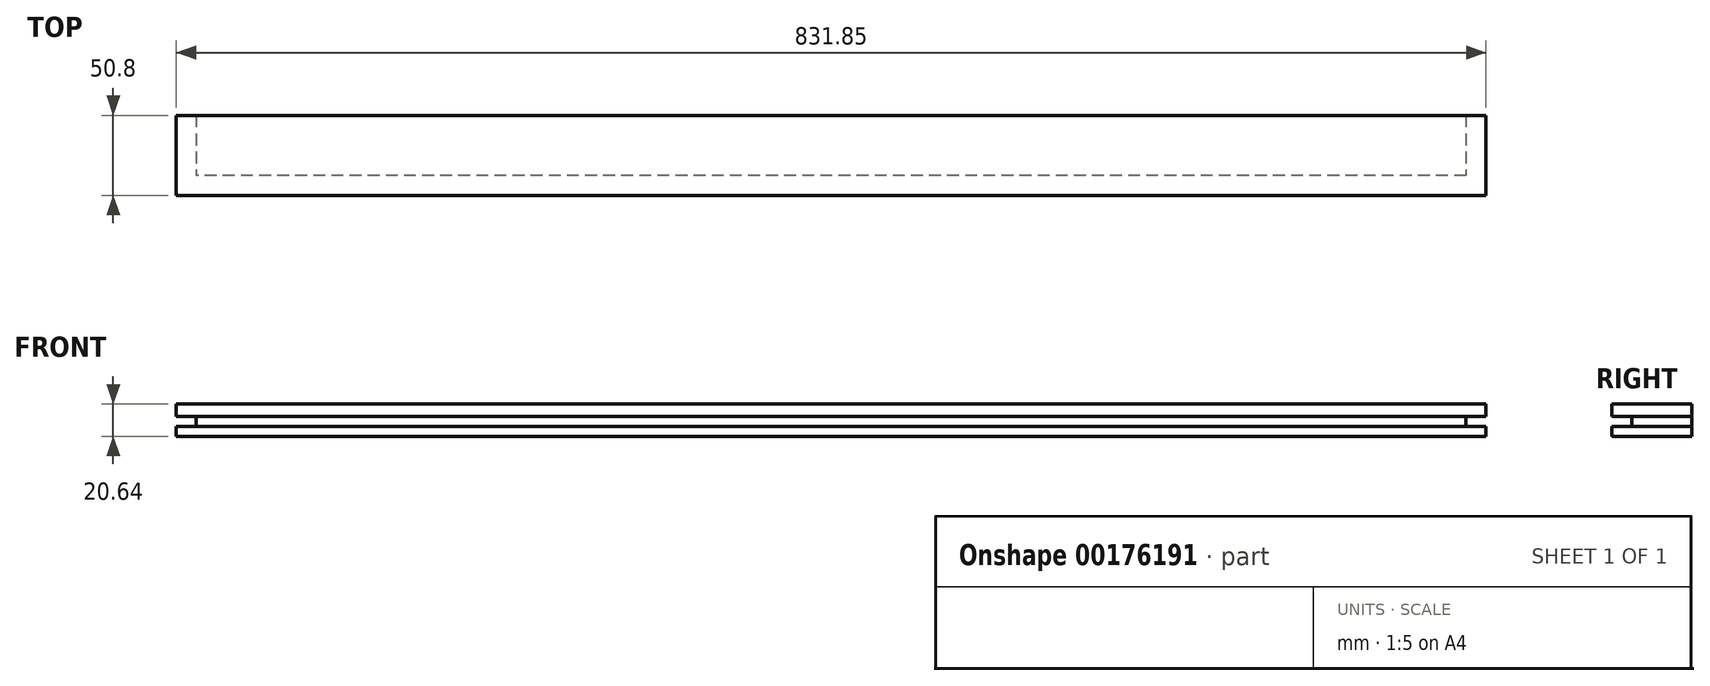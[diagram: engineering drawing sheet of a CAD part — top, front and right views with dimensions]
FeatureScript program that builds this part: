
annotation { "Feature Type Name" : "Feature", "Feature Type Description" : "" }
export const myFeature = defineFeature(function(context is Context, id is Id, definition is map)
    precondition{}
    {
        {
            var Q0;
            Q0=qCreatedBy(makeId("Top.planeOp"),FACE);
            var sketch = newSketch(context, id + "F0", { "sketchPlane" : qUnion([Q0])});
            skLineSegment(sketch, "E0.bottom", {"start": v(0, 0) * mm, "end": v(831.85, 0) * mm});
            skLineSegment(sketch, "E0.top", {"start": v(0, 50.8) * mm, "end": v(831.85, 50.8) * mm});
            skLineSegment(sketch, "E0.left", {"start": v(0, 0) * mm, "end": v(0, 50.8) * mm});
            skLineSegment(sketch, "E0.right", {"start": v(831.85, 0) * mm, "end": v(831.85, 50.8) * mm});
            skSolve(sketch);
        }
        {
            var Q0;
            Q0=makeQuery(id+"F0.imprint","IMPRINT",FACE,{"disambiguationData":[TD([[makeQuery(id+"F0.imprint","IMPRINT",EDGE,{"derivedFrom":sQuery(id+"F0.wireOp",EDGE,"E0.bottom")}),1.0]])]});
            extrude(context, id + "F1", {"entities" : qUnion([Q0]), "depth" : 20.64 * mm});
        }
        {
            var Q0;
            Q0=qCreatedBy(makeId("Right.planeOp"),FACE);
            var sketch = newSketch(context, id + "F2", { "sketchPlane" : qUnion([Q0])});
            skLineSegment(sketch, "E1.bottom", {"start": v(0, 12.7) * mm, "end": v(12.7, 12.7) * mm});
            skLineSegment(sketch, "E1.top", {"start": v(0, 6.35) * mm, "end": v(12.7, 6.35) * mm});
            skLineSegment(sketch, "E1.left", {"start": v(0, 12.7) * mm, "end": v(0, 6.35) * mm});
            skLineSegment(sketch, "E1.right", {"start": v(12.7, 12.7) * mm, "end": v(12.7, 6.35) * mm});
            skSolve(sketch);
        }
        {
            var Q0;
            Q0=makeQuery(id+"F2.imprint","IMPRINT",FACE,{"disambiguationData":[TD([[makeQuery(id+"F2.imprint","IMPRINT",EDGE,{"derivedFrom":sQuery(id+"F2.wireOp",EDGE,"E1.bottom")}),-1.0]])]});
            extrude(context, id + "F3", {"entities" : qUnion([Q0]), "operationType" : NewBodyOperationType.REMOVE, "endBound" : BoundingType.UP_TO_NEXT, "depth" : 25.4 * mm});
        }
        {
            var Q0;
            Q0=qCreatedBy(makeId("Front.planeOp"),FACE);
            var sketch = newSketch(context, id + "F4", { "sketchPlane" : qUnion([Q0])});
            skLineSegment(sketch, "E2.bottom", {"start": v(0, 12.7) * mm, "end": v(12.7, 12.7) * mm});
            skLineSegment(sketch, "E2.top", {"start": v(0, 6.35) * mm, "end": v(12.7, 6.35) * mm});
            skLineSegment(sketch, "E2.left", {"start": v(0, 12.7) * mm, "end": v(0, 6.35) * mm});
            skLineSegment(sketch, "E2.right", {"start": v(12.7, 12.7) * mm, "end": v(12.7, 6.35) * mm});
            skLineSegment(sketch, "E3.bottom", {"start": v(831.85, 12.7) * mm, "end": v(819.15, 12.7) * mm});
            skLineSegment(sketch, "E3.top", {"start": v(831.85, 6.35) * mm, "end": v(819.15, 6.35) * mm});
            skLineSegment(sketch, "E3.left", {"start": v(831.85, 12.7) * mm, "end": v(831.85, 6.35) * mm});
            skLineSegment(sketch, "E3.right", {"start": v(819.15, 12.7) * mm, "end": v(819.15, 6.35) * mm});
            skSolve(sketch);
        }
        {
            var Q0;
            Q0=makeQuery(id+"F4.imprint","IMPRINT",FACE,{"disambiguationData":[TD([[makeQuery(id+"F4.imprint","IMPRINT",EDGE,{"derivedFrom":sQuery(id+"F4.wireOp",EDGE,"E2.bottom")}),-1.0]])]});
            var Q1;
            Q1=makeQuery(id+"F4.imprint","IMPRINT",FACE,{"disambiguationData":[TD([[makeQuery(id+"F4.imprint","IMPRINT",EDGE,{"derivedFrom":sQuery(id+"F4.wireOp",EDGE,"E3.bottom")}),1.0]])]});
            extrude(context, id + "F5", {"entities" : qUnion([Q0, Q1]), "operationType" : NewBodyOperationType.REMOVE, "endBound" : BoundingType.THROUGH_ALL, "oppositeDirection" : true, "depth" : 25.4 * mm});
        }
    });
